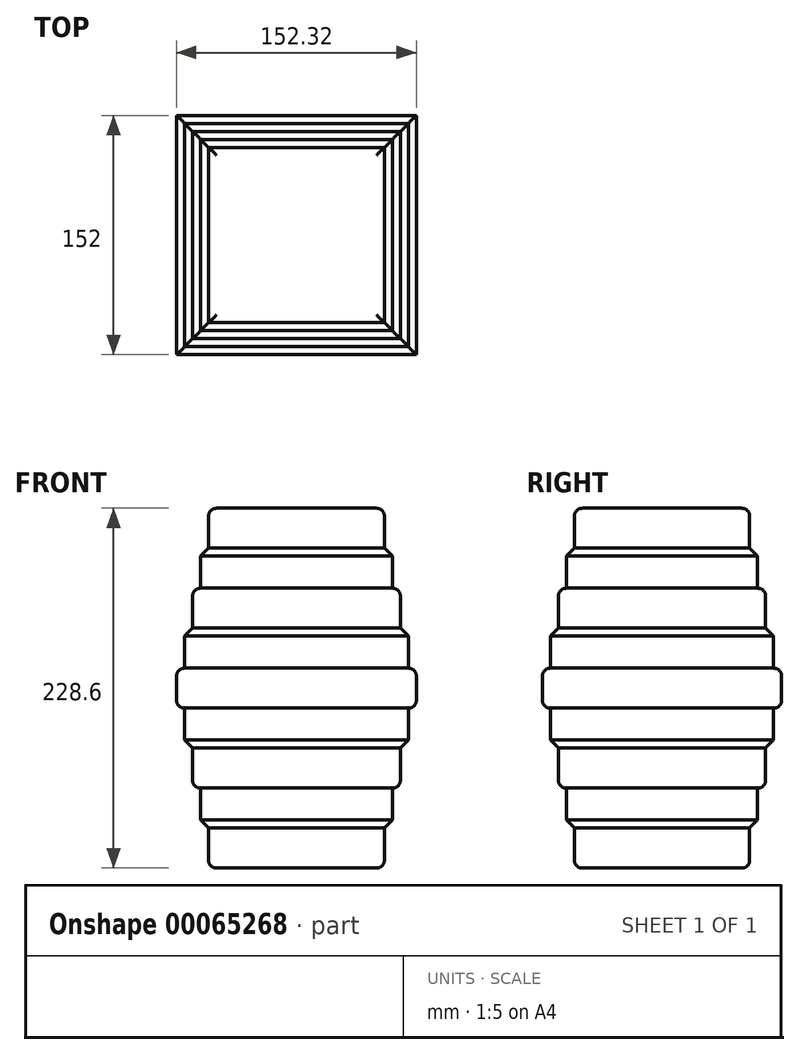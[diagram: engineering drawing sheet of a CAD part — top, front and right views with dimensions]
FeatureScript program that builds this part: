
annotation { "Feature Type Name" : "Feature", "Feature Type Description" : "" }
export const myFeature = defineFeature(function(context is Context, id is Id, definition is map)
    precondition{}
    {
        {
            var Q0;
            Q0=qCreatedBy(makeId("Top.planeOp"),FACE);
            var sketch = newSketch(context, id + "F0", { "sketchPlane" : qUnion([Q0])});
            skLineSegment(sketch, "E0.bottom", {"start": v(-75.84, 75.68) * mm, "end": v(76.48, 75.68) * mm});
            skLineSegment(sketch, "E0.top", {"start": v(-75.84, -76.32) * mm, "end": v(76.48, -76.32) * mm});
            skLineSegment(sketch, "E0.left", {"start": v(-75.84, 75.68) * mm, "end": v(-75.84, -76.32) * mm});
            skLineSegment(sketch, "E0.right", {"start": v(76.48, 75.68) * mm, "end": v(76.48, -76.32) * mm});
            skSolve(sketch);
        }
        {
            var Q0;
            Q0=makeQuery(id+"F0.imprint","IMPRINT",FACE,{"disambiguationData":[TD([[makeQuery(id+"F0.imprint","IMPRINT",EDGE,{"derivedFrom":sQuery(id+"F0.wireOp",EDGE,"E0.bottom")}),-1.0]])]});
            extrude(context, id + "F1", {"entities" : qUnion([Q0]), "depth" : 25.4 * mm});
        }
        {
            var Q0;
            Q0=makeQuery(id+"F1.opExtrude","CAP_FACE",FACE,{"disambiguationData":[OSD([sQuery(id+"F0.wireOp",EDGE,"E0.bottom"),sQuery(id+"F0.wireOp",EDGE,"E0.top"),sQuery(id+"F0.wireOp",EDGE,"E0.left"),sQuery(id+"F0.wireOp",EDGE,"E0.right")])],"isStart":false});
            fillet(context, id + "F2", {"entities" : qUnion([Q0]), "radius" : 5.08 * mm, "tangentPropagation" : true, "allowEdgeOverflow" : false});
        }
        {
            var Q0;
            Q0=makeQuery(id+"F1.opExtrude","CAP_FACE",FACE,{"disambiguationData":[OSD([sQuery(id+"F0.wireOp",EDGE,"E0.bottom"),sQuery(id+"F0.wireOp",EDGE,"E0.top"),sQuery(id+"F0.wireOp",EDGE,"E0.left"),sQuery(id+"F0.wireOp",EDGE,"E0.right")])],"isStart":true});
            fillet(context, id + "F3", {"entities" : qUnion([Q0]), "radius" : 5.08 * mm, "tangentPropagation" : true, "allowEdgeOverflow" : false});
        }
        {
            var Q0;
            Q0=makeQuery(id+"F1.opExtrude","CAP_FACE",FACE,{"disambiguationData":[OSD([sQuery(id+"F0.wireOp",EDGE,"E0.bottom"),sQuery(id+"F0.wireOp",EDGE,"E0.top"),sQuery(id+"F0.wireOp",EDGE,"E0.left"),sQuery(id+"F0.wireOp",EDGE,"E0.right")])],"isStart":true});
            extrude(context, id + "F4", {"entities" : qUnion([Q0]), "operationType" : NewBodyOperationType.ADD, "depth" : 25.4 * mm});
        }
        {
            var Q0;
            Q0=makeQuery(id+"F4.opExtrude","CAP_FACE",FACE,{"disambiguationData":[OSD([sQuery(id+"F0.wireOp",EDGE,"E0.bottom"),sQuery(id+"F0.wireOp",EDGE,"E0.top"),sQuery(id+"F0.wireOp",EDGE,"E0.left"),sQuery(id+"F0.wireOp",EDGE,"E0.right")])],"isStart":false});
            chamfer(context, id + "F5", {"entities" : qUnion([Q0]), "width" : 5.08 * mm, "tangentPropagation" : true});
        }
        {
            var Q0;
            Q0=makeQuery(id+"F1.opExtrude","CAP_FACE",FACE,{"disambiguationData":[OSD([sQuery(id+"F0.wireOp",EDGE,"E0.bottom"),sQuery(id+"F0.wireOp",EDGE,"E0.top"),sQuery(id+"F0.wireOp",EDGE,"E0.left"),sQuery(id+"F0.wireOp",EDGE,"E0.right")])],"isStart":false});
            extrude(context, id + "F6", {"entities" : qUnion([Q0]), "operationType" : NewBodyOperationType.ADD, "depth" : 25.4 * mm});
        }
        {
            var Q0;
            Q0=makeQuery(id+"F6.opExtrude","CAP_FACE",FACE,{"disambiguationData":[OSD([sQuery(id+"F0.wireOp",EDGE,"E0.bottom"),sQuery(id+"F0.wireOp",EDGE,"E0.top"),sQuery(id+"F0.wireOp",EDGE,"E0.left"),sQuery(id+"F0.wireOp",EDGE,"E0.right")])],"isStart":false});
            chamfer(context, id + "F7", {"entities" : qUnion([Q0]), "width" : 5.08 * mm, "tangentPropagation" : true});
        }
        {
            var Q0;
            Q0=makeQuery(id+"F6.opExtrude","CAP_FACE",FACE,{"disambiguationData":[OSD([sQuery(id+"F0.wireOp",EDGE,"E0.bottom"),sQuery(id+"F0.wireOp",EDGE,"E0.top"),sQuery(id+"F0.wireOp",EDGE,"E0.left"),sQuery(id+"F0.wireOp",EDGE,"E0.right")])],"isStart":false});
            extrude(context, id + "F8", {"entities" : qUnion([Q0]), "operationType" : NewBodyOperationType.ADD, "depth" : 25.4 * mm});
        }
        {
            var Q0;
            Q0=makeQuery(id+"F8.opExtrude","CAP_FACE",FACE,{"disambiguationData":[OSD([sQuery(id+"F0.wireOp",EDGE,"E0.bottom"),sQuery(id+"F0.wireOp",EDGE,"E0.top"),sQuery(id+"F0.wireOp",EDGE,"E0.left"),sQuery(id+"F0.wireOp",EDGE,"E0.right")])],"isStart":false});
            fillet(context, id + "F9", {"entities" : qUnion([Q0]), "radius" : 5.08 * mm, "tangentPropagation" : true, "allowEdgeOverflow" : false});
        }
        {
            var Q0;
            Q0=makeQuery(id+"F4.opExtrude","CAP_FACE",FACE,{"disambiguationData":[OSD([sQuery(id+"F0.wireOp",EDGE,"E0.bottom"),sQuery(id+"F0.wireOp",EDGE,"E0.top"),sQuery(id+"F0.wireOp",EDGE,"E0.left"),sQuery(id+"F0.wireOp",EDGE,"E0.right")])],"isStart":false});
            extrude(context, id + "F10", {"entities" : qUnion([Q0]), "operationType" : NewBodyOperationType.ADD, "depth" : 25.4 * mm});
        }
        {
            var Q0;
            Q0=makeQuery(id+"F10.opExtrude","CAP_FACE",FACE,{"disambiguationData":[OSD([sQuery(id+"F0.wireOp",EDGE,"E0.bottom"),sQuery(id+"F0.wireOp",EDGE,"E0.top"),sQuery(id+"F0.wireOp",EDGE,"E0.left"),sQuery(id+"F0.wireOp",EDGE,"E0.right")])],"isStart":false});
            fillet(context, id + "F11", {"entities" : qUnion([Q0]), "radius" : 5.08 * mm, "tangentPropagation" : true, "allowEdgeOverflow" : false});
        }
        {
            var Q0;
            Q0=makeQuery(id+"F10.opExtrude","CAP_FACE",FACE,{"disambiguationData":[OSD([sQuery(id+"F0.wireOp",EDGE,"E0.bottom"),sQuery(id+"F0.wireOp",EDGE,"E0.top"),sQuery(id+"F0.wireOp",EDGE,"E0.left"),sQuery(id+"F0.wireOp",EDGE,"E0.right")])],"isStart":false});
            extrude(context, id + "F12", {"entities" : qUnion([Q0]), "operationType" : NewBodyOperationType.ADD, "depth" : 25.4 * mm});
        }
        {
            var Q0;
            Q0=makeQuery(id+"F12.opExtrude","CAP_FACE",FACE,{"disambiguationData":[OSD([sQuery(id+"F0.wireOp",EDGE,"E0.bottom"),sQuery(id+"F0.wireOp",EDGE,"E0.top"),sQuery(id+"F0.wireOp",EDGE,"E0.left"),sQuery(id+"F0.wireOp",EDGE,"E0.right")])],"isStart":false});
            chamfer(context, id + "F13", {"entities" : qUnion([Q0]), "width" : 5.08 * mm, "tangentPropagation" : true});
        }
        {
            var Q0;
            Q0=makeQuery(id+"F8.opExtrude","CAP_FACE",FACE,{"disambiguationData":[OSD([sQuery(id+"F0.wireOp",EDGE,"E0.bottom"),sQuery(id+"F0.wireOp",EDGE,"E0.top"),sQuery(id+"F0.wireOp",EDGE,"E0.left"),sQuery(id+"F0.wireOp",EDGE,"E0.right")])],"isStart":false});
            extrude(context, id + "F14", {"entities" : qUnion([Q0]), "operationType" : NewBodyOperationType.ADD, "depth" : 25.4 * mm});
        }
        {
            var Q0;
            Q0=makeQuery(id+"F14.opExtrude","CAP_FACE",FACE,{"disambiguationData":[OSD([sQuery(id+"F0.wireOp",EDGE,"E0.bottom"),sQuery(id+"F0.wireOp",EDGE,"E0.top"),sQuery(id+"F0.wireOp",EDGE,"E0.left"),sQuery(id+"F0.wireOp",EDGE,"E0.right")])],"isStart":false});
            chamfer(context, id + "F15", {"entities" : qUnion([Q0]), "width" : 5.08 * mm, "tangentPropagation" : true});
        }
        {
            var Q0;
            Q0=makeQuery(id+"F14.opExtrude","CAP_FACE",FACE,{"disambiguationData":[OSD([sQuery(id+"F0.wireOp",EDGE,"E0.bottom"),sQuery(id+"F0.wireOp",EDGE,"E0.top"),sQuery(id+"F0.wireOp",EDGE,"E0.left"),sQuery(id+"F0.wireOp",EDGE,"E0.right")])],"isStart":false});
            extrude(context, id + "F16", {"entities" : qUnion([Q0]), "operationType" : NewBodyOperationType.ADD, "depth" : 25.4 * mm});
        }
        {
            var Q0;
            Q0=makeQuery(id+"F16.opExtrude","CAP_FACE",FACE,{"disambiguationData":[OSD([sQuery(id+"F0.wireOp",EDGE,"E0.bottom"),sQuery(id+"F0.wireOp",EDGE,"E0.top"),sQuery(id+"F0.wireOp",EDGE,"E0.left"),sQuery(id+"F0.wireOp",EDGE,"E0.right")])],"isStart":false});
            fillet(context, id + "F17", {"entities" : qUnion([Q0]), "radius" : 5.08 * mm, "tangentPropagation" : true, "allowEdgeOverflow" : false});
        }
        {
            var Q0;
            Q0=makeQuery(id+"F12.opExtrude","CAP_FACE",FACE,{"disambiguationData":[OSD([sQuery(id+"F0.wireOp",EDGE,"E0.bottom"),sQuery(id+"F0.wireOp",EDGE,"E0.top"),sQuery(id+"F0.wireOp",EDGE,"E0.left"),sQuery(id+"F0.wireOp",EDGE,"E0.right")])],"isStart":false});
            extrude(context, id + "F18", {"entities" : qUnion([Q0]), "operationType" : NewBodyOperationType.ADD, "depth" : 25.4 * mm});
        }
        {
            var Q0;
            Q0=makeQuery(id+"F18.opExtrude","CAP_FACE",FACE,{"disambiguationData":[OSD([sQuery(id+"F0.wireOp",EDGE,"E0.bottom"),sQuery(id+"F0.wireOp",EDGE,"E0.top"),sQuery(id+"F0.wireOp",EDGE,"E0.left"),sQuery(id+"F0.wireOp",EDGE,"E0.right")])],"isStart":false});
            fillet(context, id + "F19", {"entities" : qUnion([Q0]), "radius" : 5.08 * mm, "tangentPropagation" : true, "allowEdgeOverflow" : false});
        }
    });
